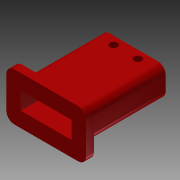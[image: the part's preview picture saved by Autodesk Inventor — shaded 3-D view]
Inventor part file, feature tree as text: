
AUTODESK INVENTOR PART (.ipt)
format: ipt  version: 2015 (Build 190159000, 159)  size: 133,632 bytes
history: native  units: in
note: dims shown in document units (in); Inventor stores cm internally (conversion verified against a paired STEP export)
features: extrude x3, sketch x3, shell x1, fillet x1
ambient origin geometry x8: Origin, YZ Plane, XZ Plane, XY Plane, X Axis, Y Axis, Z Axis, Center Point
bodies: Solid1 (feature_tree)
feature tree (8):
  extrude  "Extrusion1"  Depth=0.474in
  shell  "Shell1"  Thickness=1.25in
  extrude  "Extrusion2"  Depth=0.125in
  extrude  "Extrusion3"  Depth=0.125in
  fillet  "Fillet1"  Radius=0.5in
  sketch  "Sketch1"  dims[d0=1.0in d1=0.474in d2=1.25in d3=0.0in]
  sketch  "Sketch2"  dims[d4=0.1in d23=0.125in]
  sketch  "Sketch3"  dims[d24=0.12in d25=0.38in d26=0.5in d27=0.0in d28=0.75in d29=1.25in d30=0.125in d31=0.125in d32=0.0in d33=0.125in]
